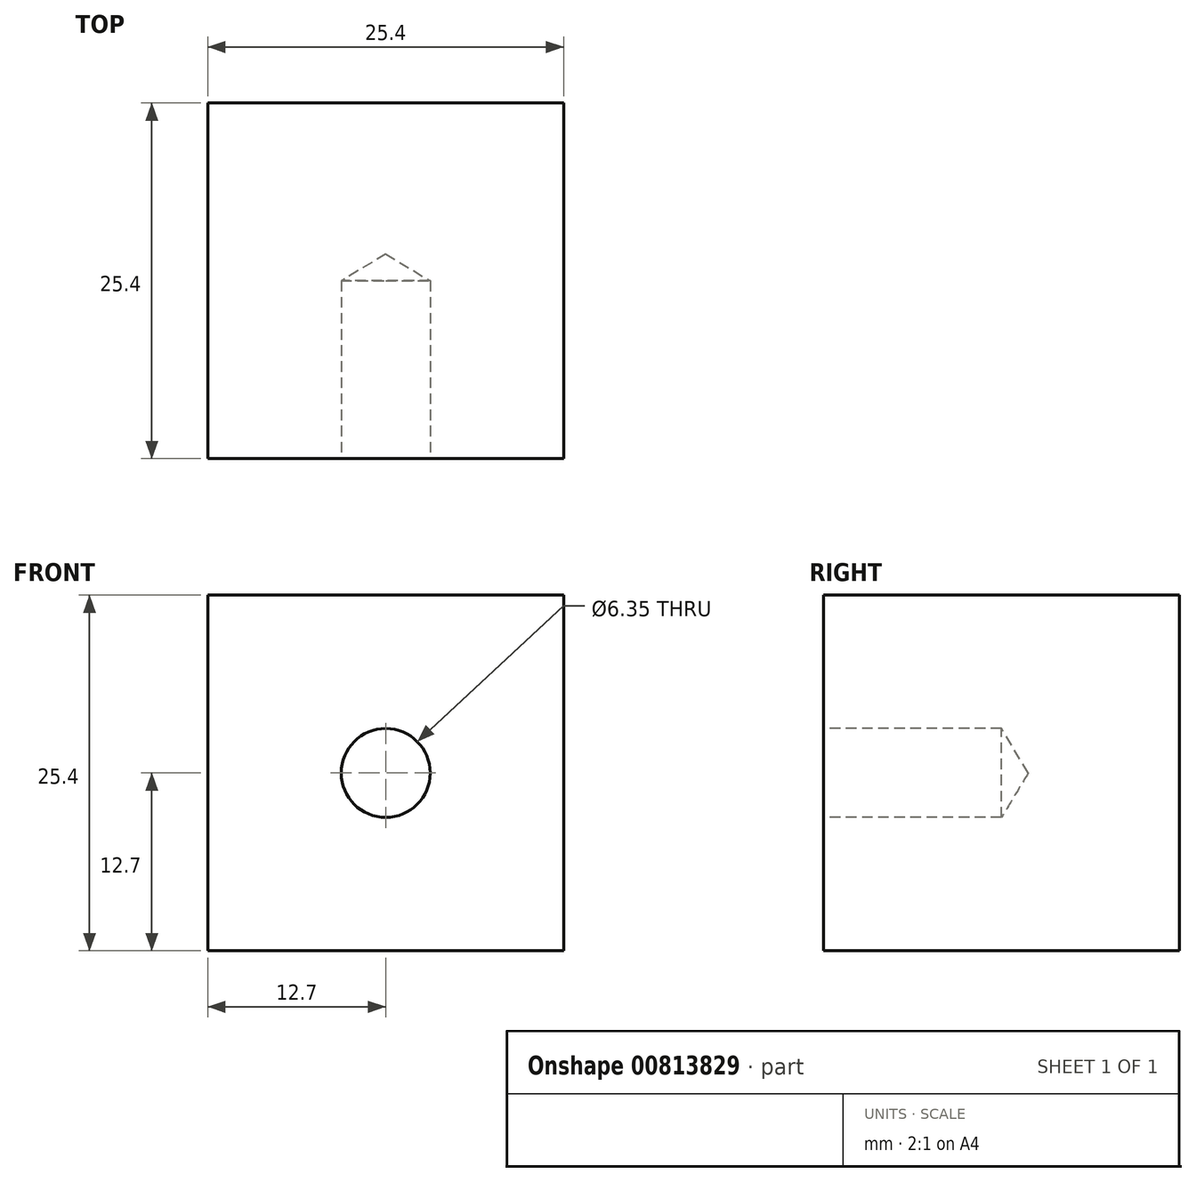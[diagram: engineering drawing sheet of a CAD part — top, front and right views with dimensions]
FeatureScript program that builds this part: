
annotation { "Feature Type Name" : "Feature", "Feature Type Description" : "" }
export const myFeature = defineFeature(function(context is Context, id is Id, definition is map)
    precondition{}
    {
        {
            var Q0;
            Q0=qCreatedBy(makeId("Front.planeOp"),FACE);
            var sketch = newSketch(context, id + "F0", { "sketchPlane" : qUnion([Q0])});
            skLineSegment(sketch, "E0.bottom", {"start": v(0, 0) * mm, "end": v(25.4, 0) * mm});
            skLineSegment(sketch, "E0.top", {"start": v(0, 25.4) * mm, "end": v(25.4, 25.4) * mm});
            skLineSegment(sketch, "E0.left", {"start": v(0, 0) * mm, "end": v(0, 25.4) * mm});
            skLineSegment(sketch, "E0.right", {"start": v(25.4, 0) * mm, "end": v(25.4, 25.4) * mm});
            skSolve(sketch);
        }
        {
            var Q0;
            Q0 = qSketchRegion(id + "F0", true);
            extrude(context, id + "F1", {"entities" : qUnion([Q0]), "depth" : 25.4 * mm, "offsetDistance" : 25.4 * mm});
        }
        {
            var Q0;
            Q0=makeQuery(id+"F1.opExtrude","CAP_FACE",FACE,{"disambiguationData":[OSD([sQuery(id+"F0.wireOp",EDGE,"E0.bottom"),sQuery(id+"F0.wireOp",EDGE,"E0.top"),sQuery(id+"F0.wireOp",EDGE,"E0.left"),sQuery(id+"F0.wireOp",EDGE,"E0.right")])],"isStart":false});
            var sketch = newSketch(context, id + "F2", { "sketchPlane" : qUnion([Q0])});
            skCircle(sketch, "E1", {"center": v(12.7, 12.7) * mm, "radius": 3.82 * mm});
            skCircle(sketch, "E2", {"center": v(12.7, 12.7) * mm, "radius": 1.97 * mm});
            skPoint(sketch, "E3", {"position": v(12.7, 25.4) * mm});
            skPoint(sketch, "E4", {"position": v(25.4, 12.7) * mm});
            skSolve(sketch);
        }
        {
            var Q0;
            Q0=sQuery(id+"F2.wireOp",VERTEX,"E1.center");
            var Q1;
            Q1=makeQuery(id+"F1.opExtrude","SWEPT_BODY",BODY,{"disambiguationData":[OSD([sQuery(id+"F0.wireOp",EDGE,"E0.bottom"),sQuery(id+"F0.wireOp",EDGE,"E0.top"),sQuery(id+"F0.wireOp",EDGE,"E0.left"),sQuery(id+"F0.wireOp",EDGE,"E0.right")])]});
            hole(context, id + "F3", {"style" : HoleStyle.SIMPLE, "endStyle" : HoleEndStyle.BLIND, "holeDiameter" : 6.35 * mm, "majorDiameter" : 6.35 * mm, "holeDepth" : 12.7 * mm, "isTappedThrough" : true, "tappedDepth" : 12.7 * mm, "tapClearance" : 3, "locations" : qUnion([Q0]), "scope" : qUnion([Q1])});
        }
    });
